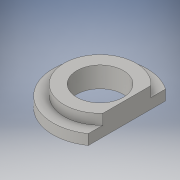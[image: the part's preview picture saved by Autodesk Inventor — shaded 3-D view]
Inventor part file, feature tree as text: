
AUTODESK INVENTOR PART (.ipt)
format: ipt  version: 2016 (Build 200138000, 138)  size: 118,784 bytes
history: native  units: in
note: dims shown in document units (in); Inventor stores cm internally (conversion verified against a paired STEP export)
features: extrude x4, sketch x4
ambient origin geometry x8: Origin, YZ Plane, XZ Plane, XY Plane, X Axis, Y Axis, Z Axis, Center Point
bodies: Solid1 (feature_tree)
feature tree (8):
  extrude  "Extrusion1"  Depth=0.048in TaperAngle=0.0deg
  extrude  "Extrusion2"  Depth=0.048in TaperAngle=0.0deg
  extrude  "Extrusion3"  Depth=0.16in TaperAngle=0.0deg
  extrude  "Extrusion4"  Depth=0.16in TaperAngle=0.0deg
  sketch  "Sketch1"  dims[d0=0.438in d1=0.048in d2=0.0in]
  sketch  "Sketch2"  dims[d3=0.335in d4=0.048in d5=0.0in]
  sketch  "Sketch3"  dims[d6=0.2165in d7=0.16in d8=0.0in]
  sketch  "Sketch4"  dims[d9=0.125in d10=0.16in d11=0.0in]
